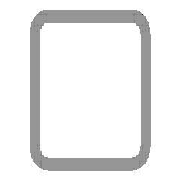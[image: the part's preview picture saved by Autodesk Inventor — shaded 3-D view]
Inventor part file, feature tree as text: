
AUTODESK INVENTOR PART (.ipt)
format: ipt  version: 2025.3 (Build 293356000, 356)  size: 155,136 bytes
history: native  units: mm (DEFAULTED — no unit token found)
features: other x4, plane x3, split x2, sketch x1
ambient origin geometry x8: Origin, YZ Plane, XZ Plane, XY Plane, X Axis, Y Axis, Z Axis, Center Point
bodies: Solid1 (feature_tree), Body (feature_tree)
feature tree (10):
  parser-record x1  (decoder bookkeeping rows leaked as tree rows — omitted from the tree; the rows remain in map.json)
  other  "Driven Length"
  other  "Start Plane"
  other  "End Plane"
  plane  "Work Plane4"
  split  "Split1"
  plane  "Work Plane5"
  split  "Split2"
  sketch  "Sketch3"  dims[d3=2216.344931mm d4=0.0mm d7=6.0mm d9=80.0mm d11=80.0mm d12=3.0mm d13=-14.545455mm d14=2201.799476mm d15=40.0mm d16=40.0mm d17=90.0deg d18=2216.344931mm]
  plane  "Work Plane3"
